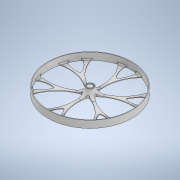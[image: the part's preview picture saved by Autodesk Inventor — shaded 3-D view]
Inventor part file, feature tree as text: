
AUTODESK INVENTOR PART (.ipt)
format: ipt  version: 2020 (Build 240168000, 168)  size: 431,616 bytes
history: native  units: mm
features: pattern_circular x5, fillet x5, extrude x4, sketch x4
ambient origin geometry x8: Origin, YZ Plane, XZ Plane, XY Plane, X Axis, Y Axis, Z Axis, Center Point
bodies: Body1 (feature_tree)
feature tree (18):
  extrude  "Extrusion2"  Depth=96.0mm
  extrude  "Extrusion3"  Depth=28.0mm
  pattern_circular  "Circular Pattern1"  [2 undecoded]
  fillet  "Fillet1"  Radius=7.5mm
  pattern_circular  "Circular Pattern2"  [2 undecoded]
  fillet  "Fillet2"  Radius=12.0mm
  pattern_circular  "Circular Pattern3"  Angle=45.0deg  [1 undecoded]
  fillet  "Fillet3"  Radius=18.0mm
  pattern_circular  "Circular Pattern4"  [2 undecoded]
  extrude  "Extrusion4"  Depth=2.0mm
  extrude  "Extrusion5"  Depth=2.0mm
  fillet  "Fillet4"  Radius=9.0mm
  fillet  "Fillet5"  Radius=9.0mm
  pattern_circular  "Circular Pattern5"  [2 undecoded]
  sketch  "Sketch1"  dims[d6=56.0mm d7=96.0mm]
  sketch  "Sketch2"  dims[d8=48.0mm d9=28.0mm]
  sketch  "Sketch3"  dims[d10=9.0mm]
  sketch  "Sketch4"  dims[d11=1.0mm d12=10.0mm d13=0.0mm d14=7.5mm d15=10.0mm d16=12.0mm d17=45.0deg d22=18.0mm d23=18.0mm d30=60.0mm d31=60.0mm d34=9.0mm d35=9.0mm d36=0.0mm d37=40.0mm d38=1.0mm d39=0.0mm d40=60.0mm d41=360.0deg d43=2.0mm d44=60.0mm d45=360.0deg d47=2.0mm d48=60.0mm d49=360.0deg d51=1.0mm d52=0.0mm d53=2.0mm d54=60.0mm d55=360.0deg d57=12.0mm d58=10.0mm d59=1.0mm d60=0.0mm d61=0.0mm d62=7.5mm d63=10.0mm d64=10.0mm d65=0.0mm d66=10.0mm d67=2.0mm d68=60.0mm d69=360.0deg]
note: 9 required parameter values undecoded (feature->parameter linkage not recoverable at this tier; creation-order binding heuristic only, values carry confidence <= 0.55)
